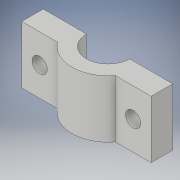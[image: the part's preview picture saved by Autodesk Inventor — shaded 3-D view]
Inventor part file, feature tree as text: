
AUTODESK INVENTOR PART (.ipt)
format: ipt  version: 2017 SP1 (Build 210196100, 196)  size: 122,880 bytes
history: native  units: in
note: dims shown in document units (in); Inventor stores cm internally (conversion verified against a paired STEP export)
features: hole x2, sketch x2, extrude x1
ambient origin geometry x8: Origin, YZ Plane, XZ Plane, XY Plane, X Axis, Y Axis, Z Axis, Center Point
bodies: Solid1 (feature_tree)
feature tree (5):
  extrude  "Extrusion1"  Depth=0.75in
  hole  "Hole1"  [1 undecoded]
  hole  "Hole2"  [1 undecoded]
  sketch  "Sketch2"  dims[d0=3.0in d1=0.75in]
  sketch  "Sketch3"  dims[d6=1.0in d7=0.0in d9=0.375in d10=0.266in d11=0.75in d12=0.507in d13=0.25in d14=0.5635in d15=1.0in d16=0.8108in d17=0.625in d18=0.625in d19=0.266in d20=0.75in d21=0.507in d22=0.25in d23=0.5635in d24=1.0in d25=0.8108in]
note: 2 required parameter values undecoded (feature->parameter linkage not recoverable at this tier; creation-order binding heuristic only, values carry confidence <= 0.55)
